# Revit family: ISI_IdealStandard_WCSeats_JasperMorrison_E6214
name_source: partatom
category: Plumbing Fixtures
revit_build: Autodesk Revit MEP 2012 (Build: 20110309_2315(x64)
units: mm (PartAtom-declared; Revit-internal decimal feet)

## types (1)
- E6214-Jasper Morrison slow closing seat and cover, quick release
    Accessories = www.idealspec.co.uk
    AreaUnits = millimeters
    Assembly Code = C1030200
    AssetType = Fixed
    BIMObjectName = ISI_IdealStandard_WCSeats_JasperMorrison_E6214
    Brand = Ideal Standard
    CWFU = 0
    Color = White
    ConnectionType = Plumbing
    Cost = 0 $
    Default Elevation = 1219 mm
    Description = Jasper morrison seat & cover, slow close, quick release
    DurationUnit = year
    ECA = No
    ExpectedLife = 15
    Features = Seat & cover, slow close, quick release
    Finish = White
    HWFU = 0
    Help = www.idealspec.co.uk/contact-us.html
    IfcExportAs = IfcSanitaryTerminalType
    IfcExportType = WCSEAT
    InstallationInstructions = www.idealspec.co.uk/resources.html
    LinearUnits = millimeters
    ManufacturerURL = www.idealspec.co.uk
    Material = Plastic
    Model = E621401
    ModelNumber = E621401
    ModelReference = Jasper morrison seat & cover, slow close, quick release
    NBSDescription = WC seats and covers
    NBSReference = 45-35-70/391
    Name = WCSeats_JasperMorrison-E6214_IdealStandard
    NettWeight = 2.7 Kg
    NominalDepth = 448 mm
    NominalHeight = 56 mm
    NominalLength = 448 mm
    NominalWidth = 366 mm
    ProductInformation = www.idealspec.co.uk/assets/datasheet/E621401
    Seat&CoverType = Slow Close
    SeatColor = White
    SeatHasCover = Yes
    SeatMaterial = Plastic
    SeatType = RingSeat
    Shape = Soft Square
    Size = 366 x 447 x 56 mm
    Space = Internal
    SpareParts = www.fastpart-spares.co.uk
    URL = www.idealspec.co.uk
    Uniclass2 = Pr_40_20_93_95
    Version = 2
    VolumeUnits = Litres
    WFU = 0
    WRAS = No
    WarrantyDescription = Manufacturers Warranty
    WarrantyDurationParts = 5
    WarrantyDurationUnit = year
    WaterEfficientProduct = No

## geometry (parser evidence)
native form markers: Sweep x3
no freeform markers — native parametric forms only
